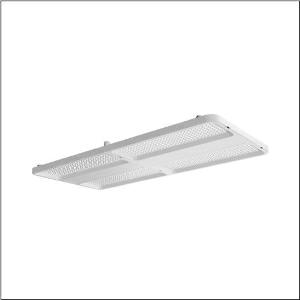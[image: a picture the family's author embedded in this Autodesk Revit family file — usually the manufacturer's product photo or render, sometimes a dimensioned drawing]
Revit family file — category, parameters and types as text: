
# Revit family: highbay_21_maxi_52hn12db4qba
name_source: partatom
category: Lighting Fixtures
units: mm (PartAtom-declared; Revit-internal decimal feet)

## family parameters
Cut with Voids When Loaded = No
Host = Face
Light Source = No
Part Type = Normal
Room Calculation Point = No
Round Connector Dimension = Use Diameter
Shared = No

## types (1)
- --- (1 x LED, 5840 lm, 31.4 W, 4000K)
    Apparent Load = 31 VA
    CIE Flux Codes = 90 98 100 100 100
    Color Rendering = 80
    Color Temperature = 4000K
    Default Elevation = 1800 mm
    Description = high bay luminaire Highbay 21 maxi; direct symmetric wide distribution, light control with lens of PMMA; UGR ≤ 22 (X = 4H | Y = 8H | S = 0.25H | reflection values 70/50/20); luminous flux: 38.000lm; light colour: 840, colour temperature: 4000K, MacAdam ≤ 3 SDCM (initial), colour rendering: CRI > 80; luminous efficacy: 192,2lm/W; rated service life: 75.000h (L80) at AT= ta max; control: DALI 2; luminaire connection: terminal, 5-pole, max. 2.5mm² (cable entry for one cable, Ø 8.5..16mm); mains connection: 230..240V, AC/DC 0/50..60Hz; connected load: 197,7W; protection rating (complete): IP40; insulation class (complete): insulation class I (protective earthing); protection symbol: D; impact resistance: IK08; certification: CE, ENEC, VDE, UKCA; luminaire for central battery installations according to EN 60598-2-22, internal wiring halogen-free; luminaire LABS conformity tested according to VDMA 24364:2018-05; ball impact resistant only with use of appropriate mounting accessories; Suitable for use in the food industry according to the specifications of IFS-Food, HACCP and/or BRC; housing frame of high-performance plastic PA6, matt traffic white (RAL 9016); cover of PMMA; dimension (LxWxH): 946 x 442 x 72mm; permissible operating ambient temperature: -40..+60°C (reducing of maximum allowable ambient temperature of 5°C with ceiling mounting); packaging unit: 1 piece; (delivery without accessories; please order mounting accessories separately)
    Height = 72 mm  [stored 0.23622 ft]
    Lamp = 1 x LED
    Lamp Light Flux = 5840 lm
    Lamp Power = 31.4 W
    Lamp count = 1
    Length = 946 mm
    Luminous efficacy = 186 lm/W
    Manufacturer = Siteco
    ModVariant = No
    Model = 52HN12DB4QBA
    Mounting Place = Ceiling
    Mounting Type = Pendant
    Number of Poles = 1
    OnlyDefault = Yes
    Power Factor = 1
    Product Name = Highbay 21 maxi
    Product group = high bay luminaire
    ProductGroupID = 902
    Protection Class = Protection class I
    Protection Degree = IP 40
    RLX_Detail_Level = 1
    RLX_Emergency_Light_Flux = 0 lm
    RLX_Emergency_Type = 0
    RLX_Emergency_Type_DB = No
    RlxData = <blob elided: 128617 chars, md5=7154df28>
    Socket = socket
    Standby Power = 0 W
    System Light Flux = 5840 lm
    System Power = 31 W
    Type Comments = : DC mode (central or group accumulator) initial emergency light level
    Type Image = l_1376023.jpg
    URL = http://relux.com
    VarID = @adj_014507
    Voltage = 0 V
    Weight = 0.00 kg
    Width = 442 mm

note: [stored X ft] marks values corroborated as IEEE doubles in the binary element streams (Revit-internal decimal feet)

## geometry (parser evidence)
native form markers: Blend x4, Sweep x11
no freeform markers — native parametric forms only
